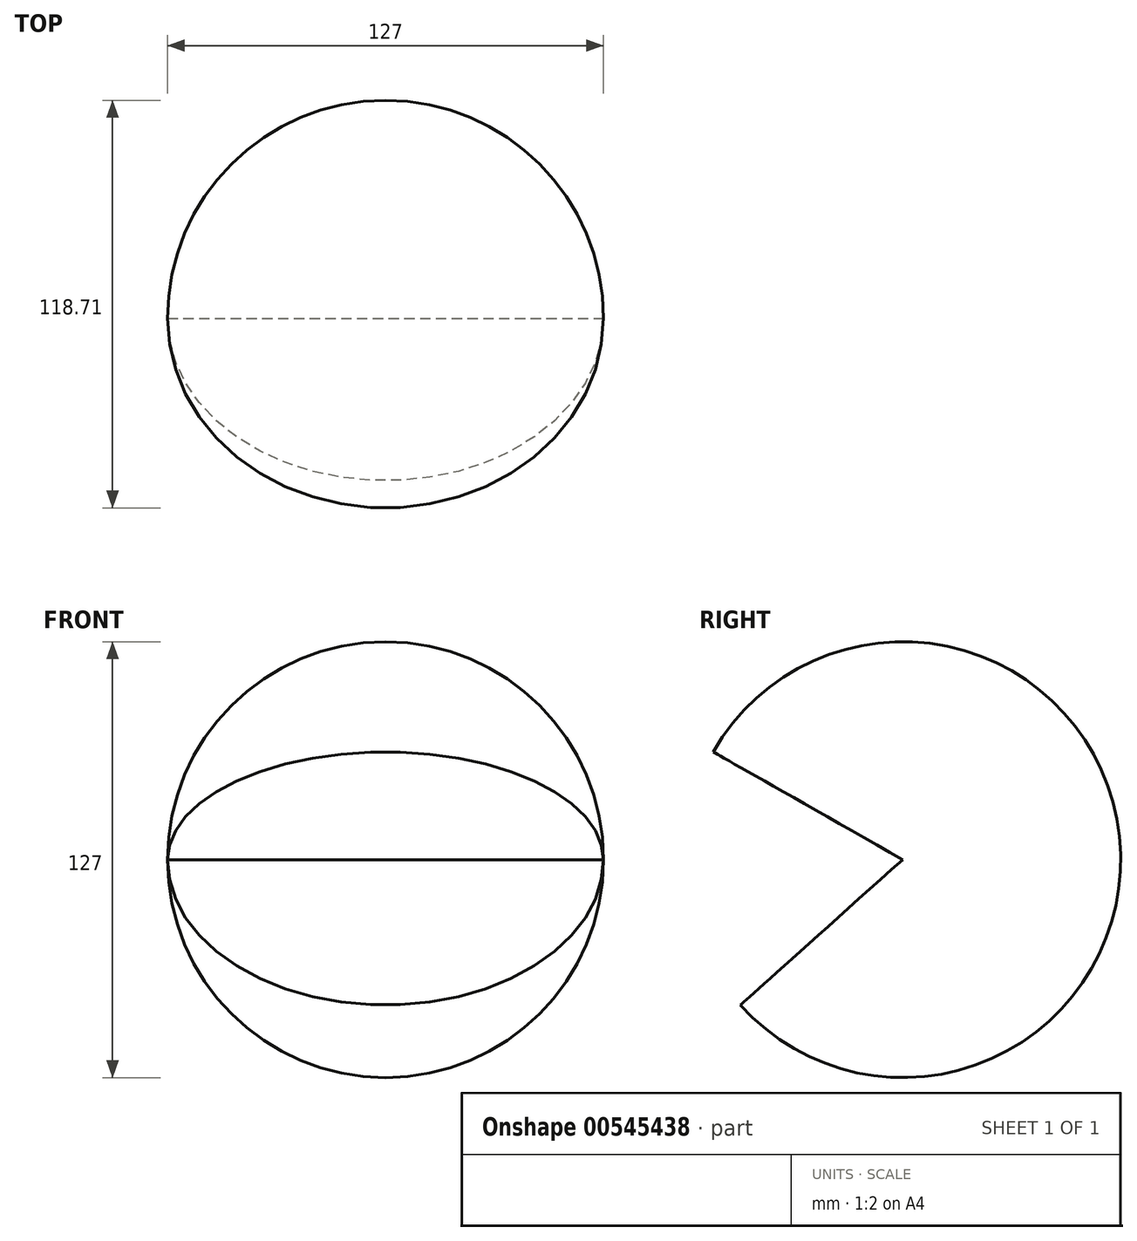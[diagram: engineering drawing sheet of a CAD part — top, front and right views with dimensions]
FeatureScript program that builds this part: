
annotation { "Feature Type Name" : "Feature", "Feature Type Description" : "" }
export const myFeature = defineFeature(function(context is Context, id is Id, definition is map)
    precondition{}
    {
        {
            var Q0;
            Q0=qCreatedBy(makeId("Front.planeOp"),FACE);
            var sketch = newSketch(context, id + "F0", { "sketchPlane" : qUnion([Q0])});
            skLineSegment(sketch, "E0", {"start": v(-63.5, 0) * mm, "end": v(63.5, 0) * mm});
            skArc(sketch, "E1", {"start": v(63.5, 0) * mm, "mid": v(0, 63.5) * mm, "end": v(-63.5, 0) * mm});
            skSolve(sketch);
        }
        {
            var Q0;
            Q0=makeQuery(id+"F0.imprint","IMPRINT",FACE,{"disambiguationData":[TD([[makeQuery(id+"F0.imprint","IMPRINT",EDGE,{"derivedFrom":sQuery(id+"F0.wireOp",EDGE,"E0")}),1.0]])]});
            var Q1;
            Q1=sQuery(id+"F0.wireOp",EDGE,"E0");
            revolve(context, id + "F1", {"entities" : qUnion([Q0]), "axis" : qUnion([Q1]), "revolveType" : RevolveType.TWO_DIRECTIONS, "oppositeDirection" : true, "angle" : 228.15 * degree, "angleBack" : 299.6 * degree});
        }
    });
